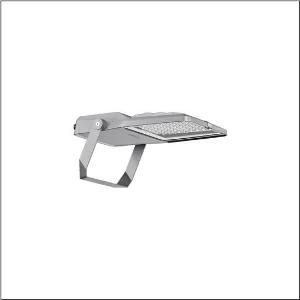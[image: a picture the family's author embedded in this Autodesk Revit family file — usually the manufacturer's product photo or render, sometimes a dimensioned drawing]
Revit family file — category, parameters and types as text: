
# Revit family: floodlight_fl_21_mini___pl61_5xa7776d2c1a_dc0d
name_source: partatom
category: Lighting Fixtures
units: mm (PartAtom-declared; Revit-internal decimal feet)

## family parameters
Cut with Voids When Loaded = No
Host = Face
Light Source = No
Part Type = Normal
Room Calculation Point = No
Round Connector Dimension = Use Diameter
Shared = No

## types (1)
- --- (1 x LED, 17510 lm, 142.9 W, 3000K)
    Apparent Load = 143 VA
    CIE Flux Codes = 33 65 98 100 100
    Color Rendering = 70
    Color Temperature = 3000K
    Default Elevation = 1800 mm
    Description = Floodlight FL 21 mini, floodlight, primary light control with lens, of PMMA, primary optical cover: protective disc, of toughened safety glass, transparent, light distribution: PL61, light emission: direct distribution, installation type: surface-mounted, LED, High Power LED, rated luminous flux: 17.510lm, luminous efficacy: 123lm/W, light colour: 730, colour temperature: 3000K, control gear: Smart Interface (Zhaga), control: flexible luminous flux parameterisation, time-dependent luminous flux control, constant luminous flux control, overheat protection, pre-setting: logarithmic dimming characteristic, with terminal, 6-pole, mains connection: 220..240V, AC, 50/60Hz, start of lifetime: 143W, end of service life: 151W, reduction: 63W, luminaire housing, of diecast aluminium, powder-coated, SITECO metallic grey (DB 702S), corrosivity category C5 mid according to DIN EN ISO 12944, suitable for swimming pools, chlorine-resistant, sealing non-destructively replaceable, mounting bracket, of steel, galvanised, powder-coated, SITECO metallic grey (DB 702S), Smart Interface below and above, protection rating (complete): IP66, insulation class (complete): insulation class II (safety insulation), certification: CE, ENEC, VDE, protection symbol: D, impact resistance: IK08, permissible operating ambient temperature: -40..+40°C, permissible operating ambient temperature for outdoor applications: -40..+50°C, standard: DIN EN 12944, LABS conformity tested according to VDMA 24364:2018-05, packaging unit: 1 piece

Light Distribution: PL61
    Height = 70 mm
    Lamp = 1 x LED
    Lamp Light Flux = 17510 lm
    Lamp Power = 142.9 W
    Lamp count = 1
    Length = 485 mm
    Luminous efficacy = 123 lm/W
    Manufacturer = Siteco
    ModVariant = No
    Model = 5XA7776D2C1A
    Mounting Place = Pole
    Mounting Type = Pole annexe
    Number of Poles = 1
    OnlyDefault = Yes
    Power Factor = 1
    Product Name = Floodlight FL 21 mini | PL61
    Product group = floodlight | pylon annexe
    ProductGroupID = 6201
    Protection Class = Protection class II
    Protection Degree = IP 66
    RLX_Detail_Level = 1
    RLX_Emergency_Light_Flux = 0 lm
    RLX_Emergency_Type = 0
    RLX_Emergency_Type_DB = No
    RlxData = <blob elided: 96397 chars, md5=36779d11>
    Socket = socket
    Standby Power = 0 W
    System Light Flux = 17510 lm
    System Power = 143 W
    Type Comments = factory setting: luminous flux: 100 % | dim-lin: 254 | 730 mA
    Type Image = l_1006845.jpg
    URL = http://relux.com
    VarID = @adj_172923
    Voltage = 0 V
    Weight = 0.00 kg
    Width = 337 mm

## geometry (parser evidence)
native form markers: Blend x4, Sweep x10
no freeform markers — native parametric forms only
